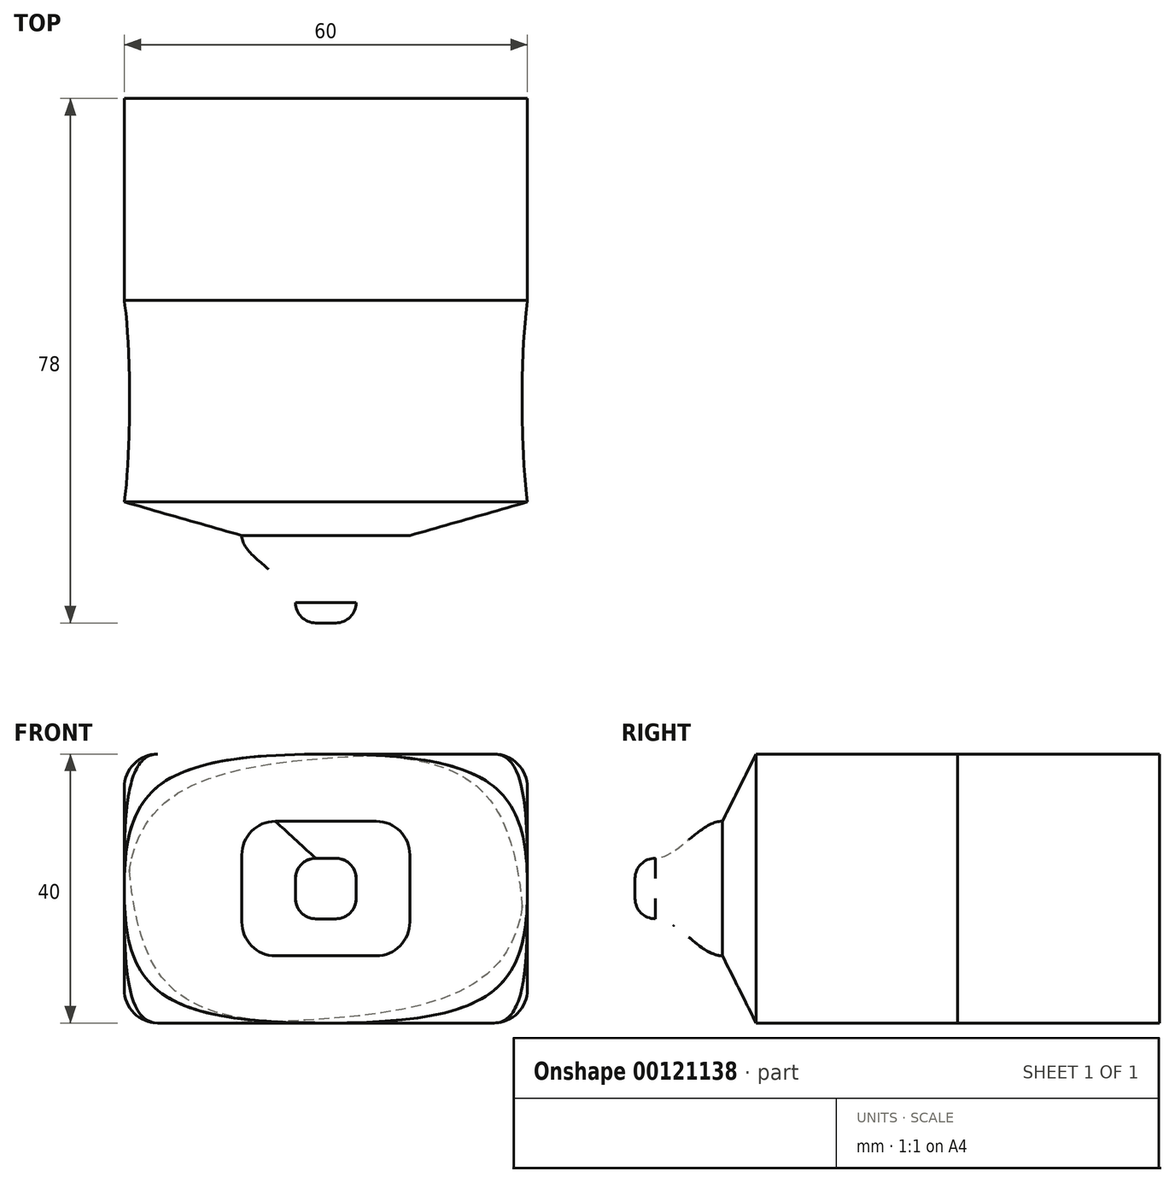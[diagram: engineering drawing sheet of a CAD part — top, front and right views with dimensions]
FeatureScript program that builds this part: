
annotation { "Feature Type Name" : "Feature", "Feature Type Description" : "" }
export const myFeature = defineFeature(function(context is Context, id is Id, definition is map)
    precondition{}
    {
        {
            var Q0;
            Q0=qCreatedBy(makeId("Front.planeOp"),FACE);
            var sketch = newSketch(context, id + "F0", { "sketchPlane" : qUnion([Q0])});
            skLineSegment(sketch, "E0.bottom", {"start": v(-1.5, 4.5) * mm, "end": v(1.5, 4.5) * mm});
            skLineSegment(sketch, "E0.top", {"start": v(-1.5, -4.5) * mm, "end": v(1.5, -4.5) * mm});
            skLineSegment(sketch, "E0.left", {"start": v(-4.5, 1.5) * mm, "end": v(-4.5, -1.5) * mm});
            skLineSegment(sketch, "E0.right", {"start": v(4.5, 1.5) * mm, "end": v(4.5, -1.5) * mm});
            skPoint(sketch, "E1.visualSharp", {"position": v(4.5, 4.5) * mm});
            skArc(sketch, "E1.filletArc", {"start": v(4.5, 1.5) * mm, "mid": v(3.62, 3.62) * mm, "end": v(1.5, 4.5) * mm});
            skPoint(sketch, "E2.visualSharp", {"position": v(-4.5, 4.5) * mm});
            skArc(sketch, "E2.filletArc", {"start": v(-1.5, 4.5) * mm, "mid": v(-3.62, 3.62) * mm, "end": v(-4.5, 1.5) * mm});
            skPoint(sketch, "E3.visualSharp", {"position": v(-4.5, -4.5) * mm});
            skArc(sketch, "E3.filletArc", {"start": v(-4.5, -1.5) * mm, "mid": v(-3.62, -3.62) * mm, "end": v(-1.5, -4.5) * mm});
            skPoint(sketch, "E4.visualSharp", {"position": v(4.5, -4.5) * mm});
            skArc(sketch, "E4.filletArc", {"start": v(1.5, -4.5) * mm, "mid": v(3.62, -3.62) * mm, "end": v(4.5, -1.5) * mm});
            skSolve(sketch);
        }
        {
            var Q0;
            Q0=qCreatedBy(makeId("Front.planeOp"),FACE);
            cPlane(context, id + "F1", {"entities" : qUnion([Q0]), "cplaneType" : CPlaneType.OFFSET, "offset" : 10 * mm, "oppositeDirection" : true, "width" : 150 * mm, "height" : 150 * mm});
        }
        {
            var Q0;
            Q0=qCreatedBy(id+"F1.planeOp",FACE);
            cPlane(context, id + "F2", {"entities" : qUnion([Q0]), "cplaneType" : CPlaneType.OFFSET, "offset" : 5 * mm, "oppositeDirection" : true, "width" : 150 * mm, "height" : 150 * mm});
        }
        {
            var Q0;
            Q0=qCreatedBy(id+"F2.planeOp",FACE);
            cPlane(context, id + "F3", {"entities" : qUnion([Q0]), "cplaneType" : CPlaneType.OFFSET, "offset" : 30 * mm, "oppositeDirection" : true, "width" : 150 * mm, "height" : 150 * mm});
        }
        {
            var Q0;
            Q0=qCreatedBy(id+"F3.planeOp",FACE);
            cPlane(context, id + "F4", {"entities" : qUnion([Q0]), "cplaneType" : CPlaneType.OFFSET, "offset" : 30 * mm, "oppositeDirection" : true, "width" : 150 * mm, "height" : 150 * mm});
        }
        {
            var Q0;
            Q0=makeQuery(id+"F0.imprint","IMPRINT",FACE,{"disambiguationData":[TD([[makeQuery(id+"F0.imprint","IMPRINT",EDGE,{"derivedFrom":sQuery(id+"F0.wireOp",EDGE,"E0.bottom")}),-1.0]])]});
            extrude(context, id + "F5", {"entities" : qUnion([Q0]), "depth" : 3 * mm});
        }
        {
            var Q0;
            Q0=makeQuery(id+"F5.opExtrude","CAP_FACE",FACE,{"disambiguationData":[OSD([sQuery(id+"F0.wireOp",EDGE,"E0.bottom"),sQuery(id+"F0.wireOp",EDGE,"E0.top"),sQuery(id+"F0.wireOp",EDGE,"E0.left"),sQuery(id+"F0.wireOp",EDGE,"E0.right"),sQuery(id+"F0.wireOp",EDGE,"E1.filletArc"),sQuery(id+"F0.wireOp",EDGE,"E2.filletArc"),sQuery(id+"F0.wireOp",EDGE,"E3.filletArc"),sQuery(id+"F0.wireOp",EDGE,"E4.filletArc")])],"isStart":false});
            fillet(context, id + "F6", {"entities" : qUnion([Q0]), "radius" : 3 * mm, "tangentPropagation" : true, "allowEdgeOverflow" : false});
        }
        {
            var Q0;
            Q0=qCreatedBy(id+"F1.planeOp",FACE);
            var sketch = newSketch(context, id + "F7", { "sketchPlane" : qUnion([Q0])});
            skLineSegment(sketch, "E5.bottom", {"start": v(-7.5, 10) * mm, "end": v(7.5, 10) * mm});
            skLineSegment(sketch, "E5.top", {"start": v(-7.5, -10) * mm, "end": v(7.5, -10) * mm});
            skLineSegment(sketch, "E5.left", {"start": v(-12.5, 5) * mm, "end": v(-12.5, -5) * mm});
            skLineSegment(sketch, "E5.right", {"start": v(12.5, 5) * mm, "end": v(12.5, -5) * mm});
            skPoint(sketch, "E6.visualSharp", {"position": v(12.5, 10) * mm});
            skArc(sketch, "E6.filletArc", {"start": v(12.5, 5) * mm, "mid": v(11.04, 8.54) * mm, "end": v(7.5, 10) * mm});
            skPoint(sketch, "E7.visualSharp", {"position": v(-12.5, 10) * mm});
            skArc(sketch, "E7.filletArc", {"start": v(-7.5, 10) * mm, "mid": v(-11.04, 8.54) * mm, "end": v(-12.5, 5) * mm});
            skPoint(sketch, "E8.visualSharp", {"position": v(-12.5, -10) * mm});
            skArc(sketch, "E8.filletArc", {"start": v(-12.5, -5) * mm, "mid": v(-11.04, -8.54) * mm, "end": v(-7.5, -10) * mm});
            skPoint(sketch, "E9.visualSharp", {"position": v(12.5, -10) * mm});
            skArc(sketch, "E9.filletArc", {"start": v(7.5, -10) * mm, "mid": v(11.04, -8.54) * mm, "end": v(12.5, -5) * mm});
            skSolve(sketch);
        }
        {
            var Q0;
            Q0=qCreatedBy(id+"F2.planeOp",FACE);
            var sketch = newSketch(context, id + "F8", { "sketchPlane" : qUnion([Q0])});
            skLineSegment(sketch, "E10.bottom", {"start": v(-25, 20) * mm, "end": v(25, 20) * mm});
            skLineSegment(sketch, "E10.top", {"start": v(-25, -20) * mm, "end": v(25, -20) * mm});
            skLineSegment(sketch, "E10.left", {"start": v(-30, 15) * mm, "end": v(-30, -15) * mm});
            skLineSegment(sketch, "E10.right", {"start": v(30, 15) * mm, "end": v(30, -15) * mm});
            skPoint(sketch, "E11.visualSharp", {"position": v(30, 20) * mm});
            skArc(sketch, "E11.filletArc", {"start": v(30, 15) * mm, "mid": v(28.54, 18.54) * mm, "end": v(25, 20) * mm});
            skPoint(sketch, "E12.visualSharp", {"position": v(-30, 20) * mm});
            skArc(sketch, "E12.filletArc", {"start": v(-25, 20) * mm, "mid": v(-28.54, 18.54) * mm, "end": v(-30, 15) * mm});
            skPoint(sketch, "E13.visualSharp", {"position": v(-30, -20) * mm});
            skArc(sketch, "E13.filletArc", {"start": v(-30, -15) * mm, "mid": v(-28.54, -18.54) * mm, "end": v(-25, -20) * mm});
            skPoint(sketch, "E14.visualSharp", {"position": v(30, -20) * mm});
            skArc(sketch, "E14.filletArc", {"start": v(25, -20) * mm, "mid": v(28.54, -18.54) * mm, "end": v(30, -15) * mm});
            skPoint(sketch, "E15", {"position": v(30, 0) * mm});
            skPoint(sketch, "E16", {"position": v(-30, 0) * mm});
            skPoint(sketch, "E17", {"position": v(0, 20) * mm});
            skPoint(sketch, "E18", {"position": v(0, -20) * mm});
            skFitSpline(sketch, "E19", {"points": [v(0, 20) * mm, v(30, 0) * mm], "startDerivative": vector(75, 0) * mm, "endDerivative": vector(0, -45) * mm});
            skFitSpline(sketch, "E20", {"points": [v(0, 20) * mm, v(-30, 0) * mm], "startDerivative": vector(-75, 0) * mm, "endDerivative": vector(0, -45) * mm});
            skFitSpline(sketch, "E21", {"points": [v(30, 0) * mm, v(0, -20) * mm], "startDerivative": vector(0, -45) * mm, "endDerivative": vector(-75, 0) * mm});
            skFitSpline(sketch, "E22", {"points": [v(-30, 0) * mm, v(0, -20) * mm], "startDerivative": vector(0, -45) * mm, "endDerivative": vector(75, 0) * mm});
            skSolve(sketch);
        }
        {
            var Q0;
            Q0=qCreatedBy(id+"F3.planeOp",FACE);
            var sketch = newSketch(context, id + "F9", { "sketchPlane" : qUnion([Q0])});
            skLineSegment(sketch, "E23.bottom", {"start": v(-25, 20) * mm, "end": v(25, 20) * mm});
            skLineSegment(sketch, "E23.top", {"start": v(-25, -20) * mm, "end": v(25, -20) * mm});
            skLineSegment(sketch, "E23.left", {"start": v(-30, 15) * mm, "end": v(-30, -15) * mm});
            skLineSegment(sketch, "E23.right", {"start": v(30, 15) * mm, "end": v(30, -15) * mm});
            skPoint(sketch, "E24.visualSharp", {"position": v(-30, 20) * mm});
            skArc(sketch, "E24.filletArc", {"start": v(-25, 20) * mm, "mid": v(-28.54, 18.54) * mm, "end": v(-30, 15) * mm});
            skPoint(sketch, "E25.visualSharp", {"position": v(30, 20) * mm});
            skArc(sketch, "E25.filletArc", {"start": v(30, 15) * mm, "mid": v(28.54, 18.54) * mm, "end": v(25, 20) * mm});
            skPoint(sketch, "E26.visualSharp", {"position": v(-30, -20) * mm});
            skArc(sketch, "E26.filletArc", {"start": v(-30, -15) * mm, "mid": v(-28.54, -18.54) * mm, "end": v(-25, -20) * mm});
            skPoint(sketch, "E27.visualSharp", {"position": v(30, -20) * mm});
            skArc(sketch, "E27.filletArc", {"start": v(25, -20) * mm, "mid": v(28.54, -18.54) * mm, "end": v(30, -15) * mm});
            skPoint(sketch, "E28", {"position": v(30, 0) * mm});
            skPoint(sketch, "E29", {"position": v(-30, 0) * mm});
            skFitSpline(sketch, "E30", {"points": [v(25, 20) * mm, v(30, 0) * mm, v(25, -20) * mm], "startDerivative": vector(30, 0) * mm, "endDerivative": vector(-30, 0) * mm});
            skFitSpline(sketch, "E31", {"points": [v(-25, 20) * mm, v(-30, 0) * mm, v(-25, -20) * mm], "startDerivative": vector(-30, 0) * mm, "endDerivative": vector(30, 0) * mm});
            skSolve(sketch);
        }
        {
            var Q0;
            Q0=qCreatedBy(id+"F4.planeOp",FACE);
            var sketch = newSketch(context, id + "F10", { "sketchPlane" : qUnion([Q0])});
            skLineSegment(sketch, "E32.bottom", {"start": v(-25, 20) * mm, "end": v(25, 20) * mm});
            skLineSegment(sketch, "E32.top", {"start": v(-25, -20) * mm, "end": v(25, -20) * mm});
            skLineSegment(sketch, "E32.left", {"start": v(-30, 15) * mm, "end": v(-30, -15) * mm});
            skLineSegment(sketch, "E32.right", {"start": v(30, 15) * mm, "end": v(30, -15) * mm});
            skPoint(sketch, "E32.middle", {"position": v(0, 0) * mm});
            skPoint(sketch, "E33.visualSharp", {"position": v(-30, 20) * mm});
            skArc(sketch, "E33.filletArc", {"start": v(-25, 20) * mm, "mid": v(-28.54, 18.54) * mm, "end": v(-30, 15) * mm});
            skPoint(sketch, "E34.visualSharp", {"position": v(30, 20) * mm});
            skArc(sketch, "E34.filletArc", {"start": v(30, 15) * mm, "mid": v(28.54, 18.54) * mm, "end": v(25, 20) * mm});
            skPoint(sketch, "E35.visualSharp", {"position": v(30, -20) * mm});
            skArc(sketch, "E35.filletArc", {"start": v(25, -20) * mm, "mid": v(28.54, -18.54) * mm, "end": v(30, -15) * mm});
            skPoint(sketch, "E36.visualSharp", {"position": v(-30, -20) * mm});
            skArc(sketch, "E36.filletArc", {"start": v(-30, -15) * mm, "mid": v(-28.54, -18.54) * mm, "end": v(-25, -20) * mm});
            skSolve(sketch);
        }
        {
            var Q1;
            Q1=makeQuery(id+"F7.imprint","IMPRINT",FACE,{"disambiguationData":[TD([[makeQuery(id+"F7.imprint","IMPRINT",EDGE,{"derivedFrom":sQuery(id+"F7.wireOp",EDGE,"E5.bottom")}),-1.0]])]});
            var Q2;
            Q2=makeQuery(id+"F0.imprint","IMPRINT",FACE,{"disambiguationData":[TD([[makeQuery(id+"F0.imprint","IMPRINT",EDGE,{"derivedFrom":sQuery(id+"F0.wireOp",EDGE,"E0.bottom")}),-1.0]])]});
            loft(context, id + "F11", {"operationType" : NewBodyOperationType.ADD, "startCondition" : LoftEndDerivativeType.NORMAL_TO_PROFILE, "startMagnitude" : 1, "endCondition" : LoftEndDerivativeType.NORMAL_TO_PROFILE, "endMagnitude" : 1, "sheetProfilesArray" : [{ "sheetProfileEntities" : qUnion([Q1]) }, { "sheetProfileEntities" : qUnion([Q2]) }]});
        }
        {
            var Q1;
            Q1=makeQuery(id+"F8.imprint","IMPRINT",FACE,{"disambiguationData":[TD([[makeQuery(id+"F8.imprint","IMPRINT",EDGE,{"derivedFrom":sQuery(id+"F8.wireOp",EDGE,"E19")}),-1.0]])]});
            var Q2;
            Q2=makeQuery(id+"F7.imprint","IMPRINT",FACE,{"disambiguationData":[TD([[makeQuery(id+"F7.imprint","IMPRINT",EDGE,{"derivedFrom":sQuery(id+"F7.wireOp",EDGE,"E5.bottom")}),-1.0]])]});
            loft(context, id + "F12", {"operationType" : NewBodyOperationType.ADD, "sheetProfilesArray" : [{ "sheetProfileEntities" : qUnion([Q1]) }, { "sheetProfileEntities" : qUnion([Q2]) }]});
        }
        {
            var Q0;
            Q0=makeQuery(id+"F8.imprint","IMPRINT",FACE,{"disambiguationData":[TD([[makeQuery(id+"F8.imprint","IMPRINT",EDGE,{"derivedFrom":sQuery(id+"F8.wireOp",EDGE,"E19")}),-1.0]])]});
            var Q1;
            {var subQ3=sQuery(id+"F9.wireOp",EDGE,"E23.bottom");Q1=makeQuery(id+"F9.imprint","IMPRINT",FACE,{"disambiguationData":[TD([[makeQuery(id+"F9.imprint","IMPRINT",EDGE,{"derivedFrom":subQ3}),-1.0]])]});}
            loft(context, id + "F13", {"sheetProfilesArray" : [{ "sheetProfileEntities" : qUnion([Q0]) }, { "sheetProfileEntities" : qUnion([Q1]) }]});
        }
        {
            var Q1;
            {var subQ3=sQuery(id+"F9.wireOp",EDGE,"E23.bottom");Q1=makeQuery(id+"F9.imprint","IMPRINT",FACE,{"disambiguationData":[TD([[makeQuery(id+"F9.imprint","IMPRINT",EDGE,{"derivedFrom":subQ3}),-1.0]])]});}
            var Q2;
            Q2=makeQuery(id+"F10.imprint","IMPRINT",FACE,{"disambiguationData":[TD([[makeQuery(id+"F10.imprint","IMPRINT",EDGE,{"derivedFrom":sQuery(id+"F10.wireOp",EDGE,"E32.bottom")}),-1.0]])]});
            loft(context, id + "F14", {"operationType" : NewBodyOperationType.ADD, "sheetProfilesArray" : [{ "sheetProfileEntities" : qUnion([Q1]) }, { "sheetProfileEntities" : qUnion([Q2]) }]});
        }
    });
